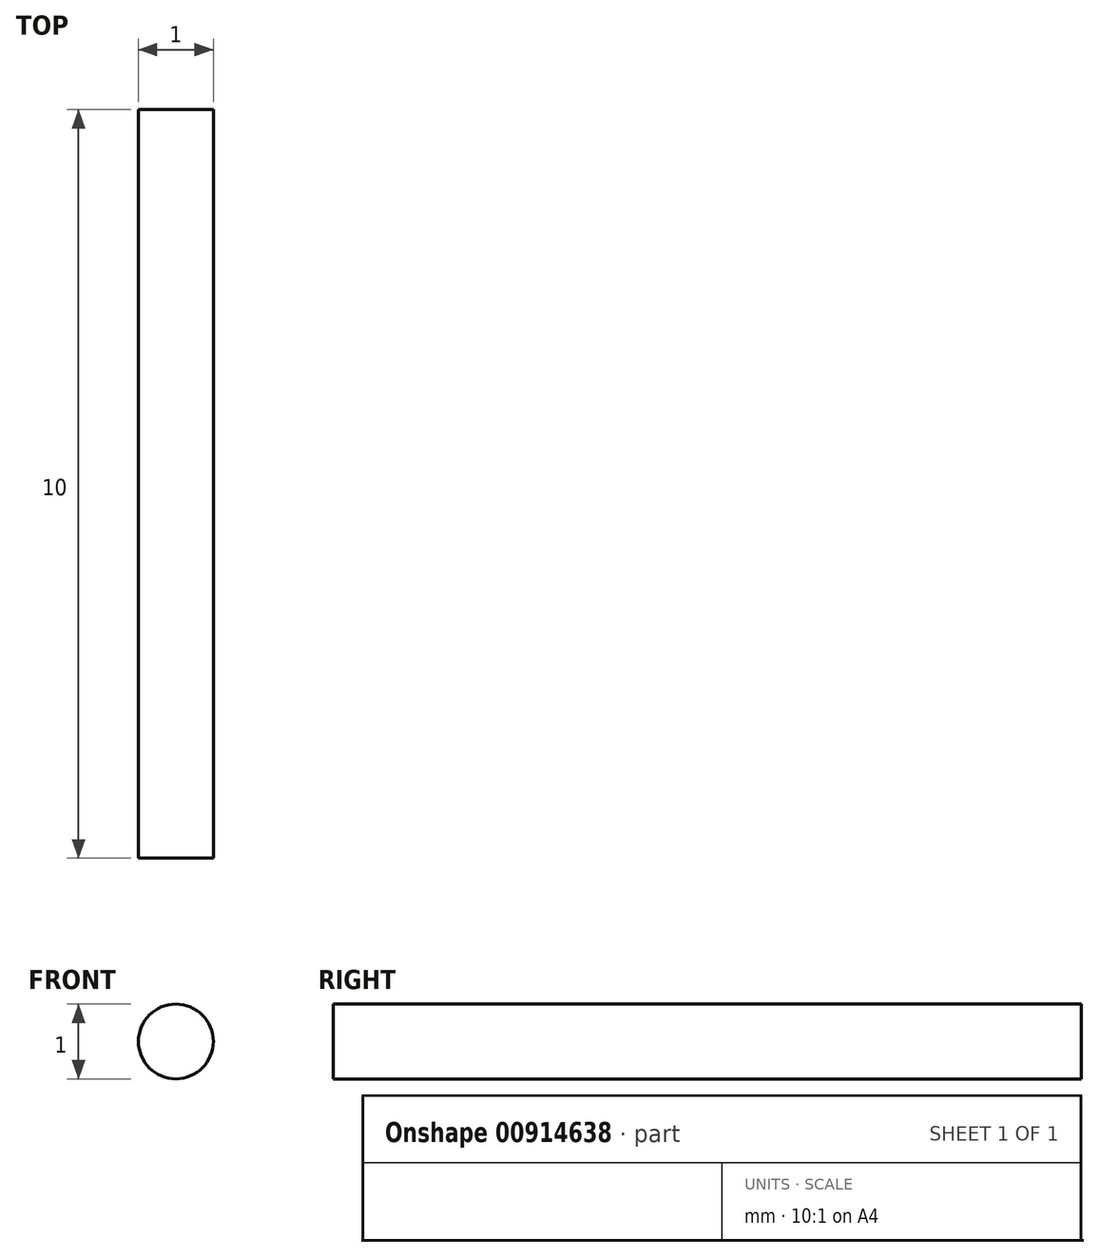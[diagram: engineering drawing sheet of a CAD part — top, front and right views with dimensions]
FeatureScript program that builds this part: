
annotation { "Feature Type Name" : "Feature", "Feature Type Description" : "" }
export const myFeature = defineFeature(function(context is Context, id is Id, definition is map)
    precondition{}
    {
        {
            var Q0;
            Q0=qCreatedBy(makeId("Front.planeOp"),FACE);
            var sketch = newSketch(context, id + "F0", { "sketchPlane" : qUnion([Q0])});
            skCircle(sketch, "E0", {"center": v(0, 0) * mm, "radius": 0.5 * mm});
            skSolve(sketch);
        }
        {
            var Q0;
            Q0 = qSketchRegion(id + "F0", true);
            extrude(context, id + "F1", {"entities" : qUnion([Q0]), "depth" : 10 * mm, "offsetDistance" : 25 * mm});
        }
    });
